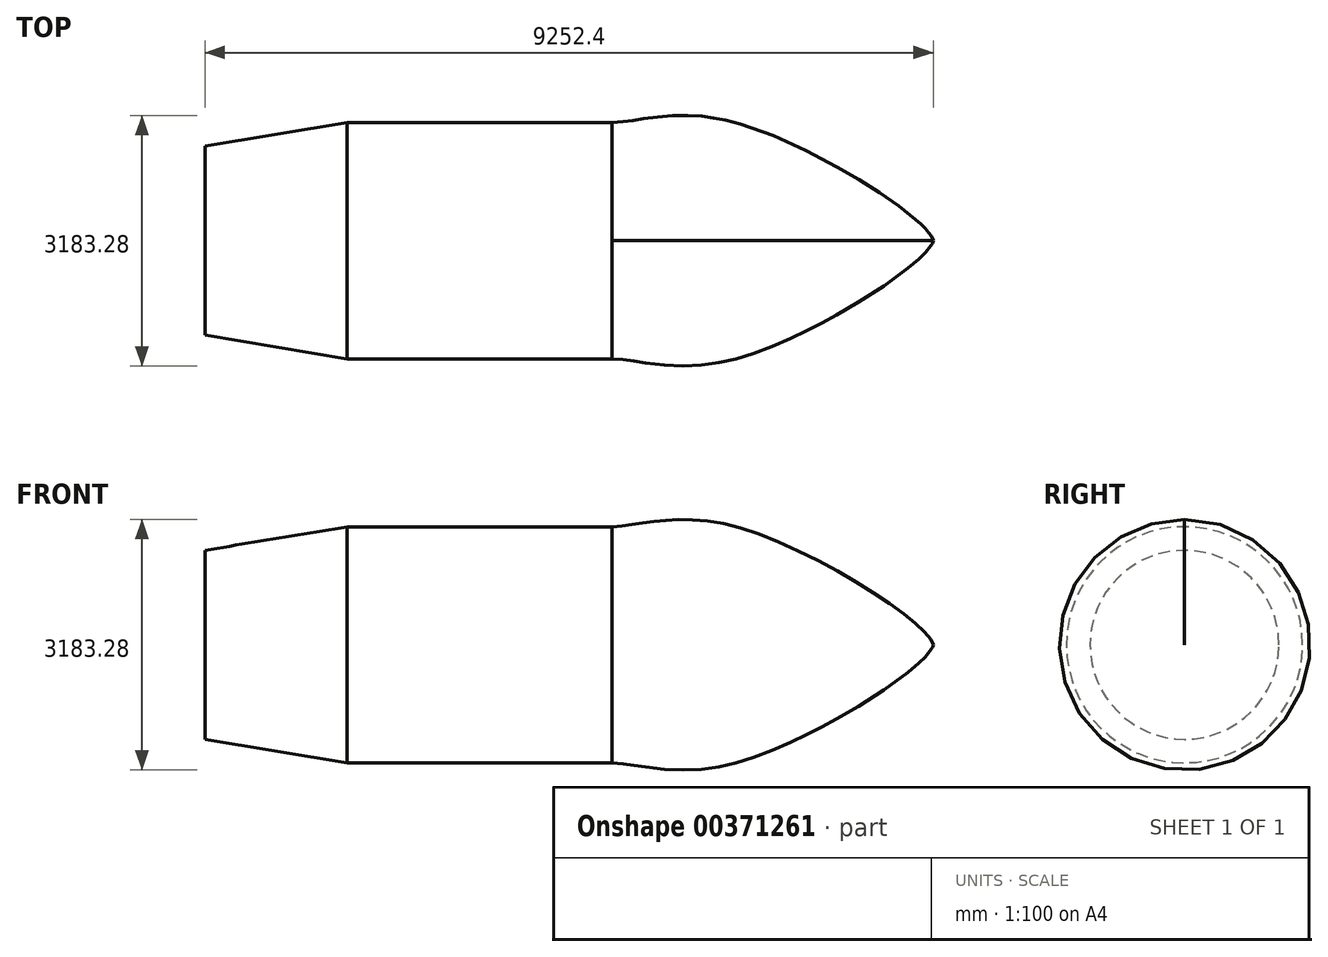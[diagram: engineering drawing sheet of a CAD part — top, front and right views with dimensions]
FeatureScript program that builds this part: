
annotation { "Feature Type Name" : "Feature", "Feature Type Description" : "" }
export const myFeature = defineFeature(function(context is Context, id is Id, definition is map)
    precondition{}
    {
        {
            var Q0;
            Q0=qCreatedBy(makeId("Front.planeOp"),FACE);
            var sketch = newSketch(context, id + "F0", { "sketchPlane" : qUnion([Q0])});
            skLineSegment(sketch, "E0", {"start": v(0, 0) * mm, "end": v(9252.4, 0) * mm});
            skLineSegment(sketch, "E1", {"start": v(0, 0) * mm, "end": v(0, 1200) * mm});
            skLineSegment(sketch, "E2", {"start": v(0, 1200) * mm, "end": v(1809.47, 1500) * mm});
            skLineSegment(sketch, "E3", {"start": v(1809.47, 1500) * mm, "end": v(5174.38, 1500) * mm});
            skFitSpline(sketch, "E4", {"points": [v(5174.38, 1500) * mm, v(6745.6, 1500) * mm, v(9252.4, 0) * mm], "startDerivative": vector(2760.59, 126.2) * mm, "endDerivative": vector(198.12, -1369.57) * mm});
            skSolve(sketch);
        }
        {
            var Q0;
            Q0 = qSketchRegion(id + "F0", true);
            var Q1;
            Q1=sQuery(id+"F0.wireOp",EDGE,"E0");
            revolve(context, id + "F1", {"entities" : qUnion([Q0]), "axis" : qUnion([Q1]), "revolveType" : RevolveType.FULL});
        }
    });
